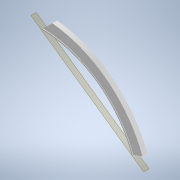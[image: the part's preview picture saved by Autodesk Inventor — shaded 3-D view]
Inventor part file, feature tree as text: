
AUTODESK INVENTOR PART (.ipt)
format: ipt  version: 2021.1 (Build 251245010, 245A)  size: 693,248 bytes
history: native  units: in
note: dims shown in document units (in); Inventor stores cm internally (conversion verified against a paired STEP export)
features: other x3, sketch x3, plane x1
ambient origin geometry x8: Origin, YZ Plane, XZ Plane, XY Plane, X Axis, Y Axis, Z Axis, Center Point
bodies: Solid1 (feature_tree)
feature tree (7):
  other  "SideA.ipt"
  other  "Solid1::SideA.ipt"
  other  "TaggingFeature1"
  sketch  "Sketch1"  dims[d0=0.3937in]
  sketch  "Sketch2"
  sketch  "Sketch5"
  plane  "Work Plane1"
